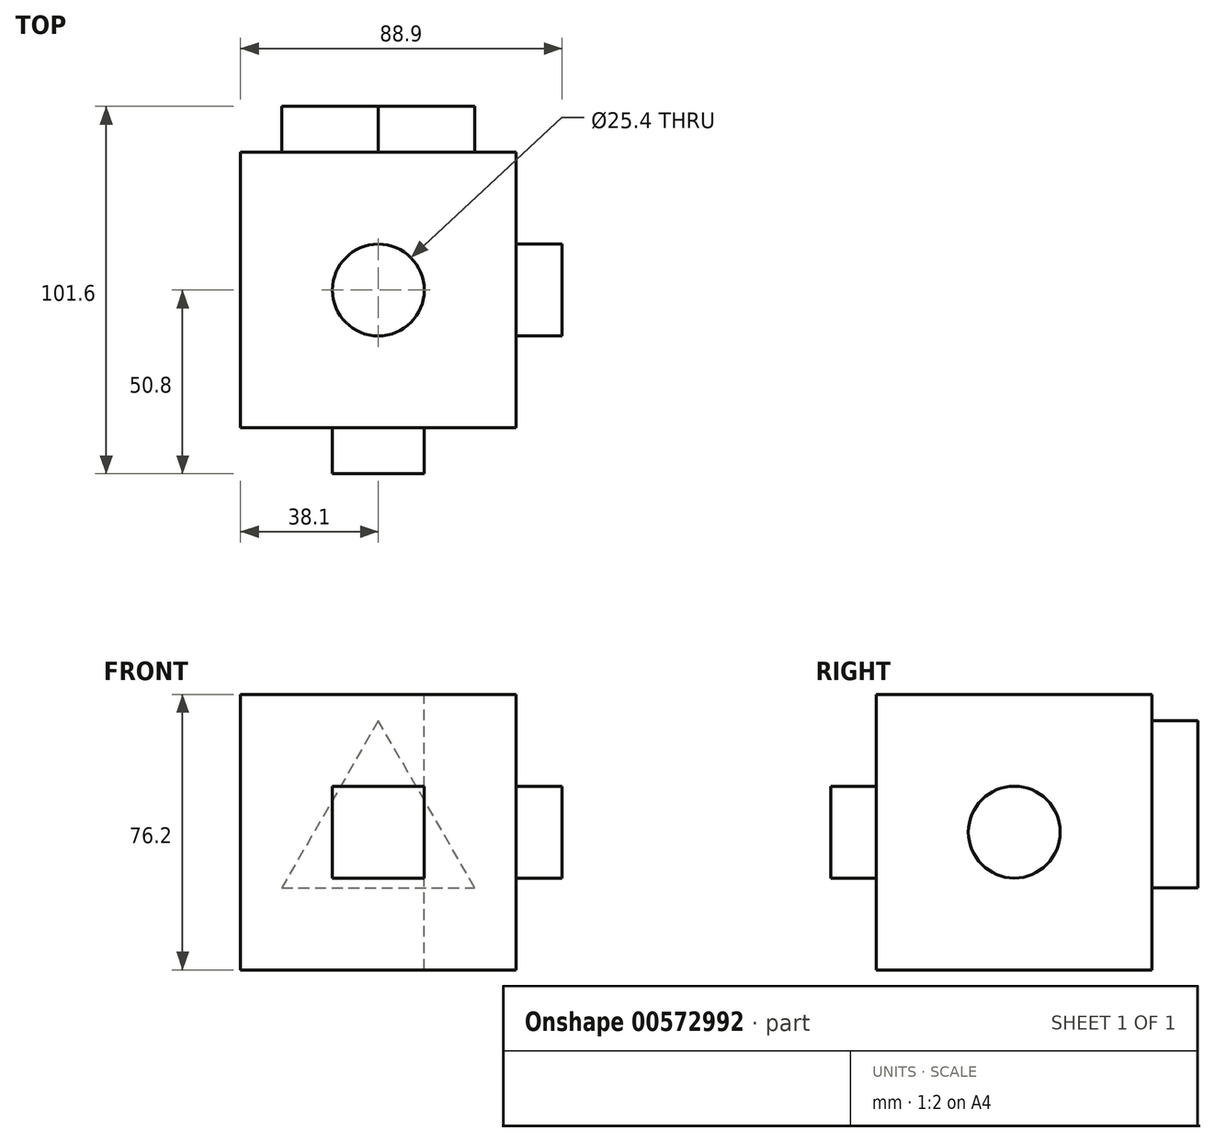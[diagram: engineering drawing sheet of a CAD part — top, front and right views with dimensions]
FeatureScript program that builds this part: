
annotation { "Feature Type Name" : "Feature", "Feature Type Description" : "" }
export const myFeature = defineFeature(function(context is Context, id is Id, definition is map)
    precondition{}
    {
        {
            var Q0;
            Q0=qCreatedBy(makeId("Front.planeOp"),FACE);
            var sketch = newSketch(context, id + "F0", { "sketchPlane" : qUnion([Q0])});
            skLineSegment(sketch, "E0.bottom", {"start": v(-76.2, 87.72) * mm, "end": v(0, 87.72) * mm});
            skLineSegment(sketch, "E0.top", {"start": v(-76.2, 11.52) * mm, "end": v(0, 11.52) * mm});
            skLineSegment(sketch, "E0.left", {"start": v(-76.2, 87.72) * mm, "end": v(-76.2, 11.52) * mm});
            skLineSegment(sketch, "E0.right", {"start": v(0, 87.72) * mm, "end": v(0, 11.52) * mm});
            skSolve(sketch);
        }
        {
            var Q0;
            Q0=makeQuery(id+"F0.imprint","IMPRINT",FACE,{"disambiguationData":[TD([[makeQuery(id+"F0.imprint","IMPRINT",EDGE,{"derivedFrom":sQuery(id+"F0.wireOp",EDGE,"E0.bottom")}),-1.0]])]});
            extrude(context, id + "F1", {"entities" : qUnion([Q0]), "depth" : 76.2 * mm, "offsetDistance" : 25.4 * mm});
        }
        {
            var Q0;
            Q0=makeQuery(id+"F1.opExtrude","CAP_FACE",FACE,{"disambiguationData":[OSD([sQuery(id+"F0.wireOp",EDGE,"E0.bottom"),sQuery(id+"F0.wireOp",EDGE,"E0.top"),sQuery(id+"F0.wireOp",EDGE,"E0.left"),sQuery(id+"F0.wireOp",EDGE,"E0.right")])],"isStart":false});
            var sketch = newSketch(context, id + "F2", { "sketchPlane" : qUnion([Q0])});
            skLineSegment(sketch, "E1.bottom", {"start": v(-50.8, 62.32) * mm, "end": v(-25.4, 62.32) * mm});
            skLineSegment(sketch, "E1.top", {"start": v(-50.8, 36.92) * mm, "end": v(-25.4, 36.92) * mm});
            skLineSegment(sketch, "E1.left", {"start": v(-50.8, 62.32) * mm, "end": v(-50.8, 36.92) * mm});
            skLineSegment(sketch, "E1.right", {"start": v(-25.4, 62.32) * mm, "end": v(-25.4, 36.92) * mm});
            skSolve(sketch);
        }
        {
            var Q0;
            Q0=makeQuery(id+"F2.imprint","IMPRINT",FACE,{"disambiguationData":[TD([[makeQuery(id+"F2.imprint","IMPRINT",EDGE,{"derivedFrom":sQuery(id+"F2.wireOp",EDGE,"E1.bottom")}),-1.0]])]});
            extrude(context, id + "F3", {"entities" : qUnion([Q0]), "operationType" : NewBodyOperationType.ADD, "depth" : 12.7 * mm, "offsetDistance" : 25.4 * mm});
        }
        {
            var Q0;
            Q0=makeQuery(id+"F1.opExtrude","SWEPT_FACE",FACE,{"disambiguationData":[OSD([sQuery(id+"F0.wireOp",EDGE,"E0.right")])]});
            var sketch = newSketch(context, id + "F4", { "sketchPlane" : qUnion([Q0])});
            skCircle(sketch, "E2", {"center": v(-38.1, 49.62) * mm, "radius": 12.7 * mm});
            skSolve(sketch);
        }
        {
            var Q0;
            Q0=makeQuery(id+"F4.imprint","IMPRINT",FACE,{"disambiguationData":[TD([[makeQuery(id+"F4.imprint","IMPRINT",EDGE,{"derivedFrom":sQuery(id+"F4.wireOp",EDGE,"E2")}),1.0]])]});
            extrude(context, id + "F5", {"entities" : qUnion([Q0]), "operationType" : NewBodyOperationType.ADD, "depth" : 12.7 * mm, "offsetDistance" : 25.4 * mm});
        }
        {
            var Q0;
            Q0=makeQuery(id+"F1.opExtrude","SWEPT_FACE",FACE,{"disambiguationData":[OSD([sQuery(id+"F0.wireOp",EDGE,"E0.bottom")])]});
            var sketch = newSketch(context, id + "F6", { "sketchPlane" : qUnion([Q0])});
            skPoint(sketch, "E3", {"position": v(-38.1, -38.1) * mm});
            skSolve(sketch);
        }
        {
            var Q0;
            Q0=sQuery(id+"F6.wireOp",VERTEX,"E3");
            var Q1;
            Q1=makeQuery(id+"F1.opExtrude","SWEPT_BODY",BODY,{"disambiguationData":[OSD([sQuery(id+"F0.wireOp",EDGE,"E0.bottom"),sQuery(id+"F0.wireOp",EDGE,"E0.top"),sQuery(id+"F0.wireOp",EDGE,"E0.left"),sQuery(id+"F0.wireOp",EDGE,"E0.right")])]});
            hole(context, id + "F7", {"style" : HoleStyle.SIMPLE, "endStyle" : HoleEndStyle.THROUGH, "holeDiameter" : 25.4 * mm, "isTappedThrough" : true, "tappedDepth" : 12.7 * mm, "tapClearance" : 3, "locations" : qUnion([Q0]), "scope" : qUnion([Q1])});
        }
        {
            var Q0;
            Q0=makeQuery(id+"F1.opExtrude","CAP_FACE",FACE,{"disambiguationData":[OSD([sQuery(id+"F0.wireOp",EDGE,"E0.bottom"),sQuery(id+"F0.wireOp",EDGE,"E0.top"),sQuery(id+"F0.wireOp",EDGE,"E0.left"),sQuery(id+"F0.wireOp",EDGE,"E0.right")])],"isStart":true});
            var sketch = newSketch(context, id + "F8", { "sketchPlane" : qUnion([Q0])});
            skCircle(sketch, "E4.cCircle", {"center": v(38.1, 49.62) * mm, "radius": 15.4 * mm, "construction": true});
            skLineSegment(sketch, "E4.0", {"start": v(64.77, 34.22) * mm, "end": v(11.43, 34.22) * mm});
            skLineSegment(sketch, "E4.1", {"start": v(11.43, 34.22) * mm, "end": v(38.1, 80.42) * mm});
            skLineSegment(sketch, "E4.2", {"start": v(38.1, 80.42) * mm, "end": v(64.77, 34.22) * mm});
            skPoint(sketch, "E4.0.midPoint", {"position": v(38.1, 34.22) * mm});
            skSolve(sketch);
        }
        {
            var Q0;
            Q0=makeQuery(id+"F8.imprint","IMPRINT",FACE,{"disambiguationData":[TD([[makeQuery(id+"F8.imprint","IMPRINT",EDGE,{"derivedFrom":sQuery(id+"F8.wireOp",EDGE,"E4.0")}),-1.0]])]});
            extrude(context, id + "F9", {"entities" : qUnion([Q0]), "operationType" : NewBodyOperationType.ADD, "depth" : 12.7 * mm, "offsetDistance" : 25.4 * mm});
        }
    });
